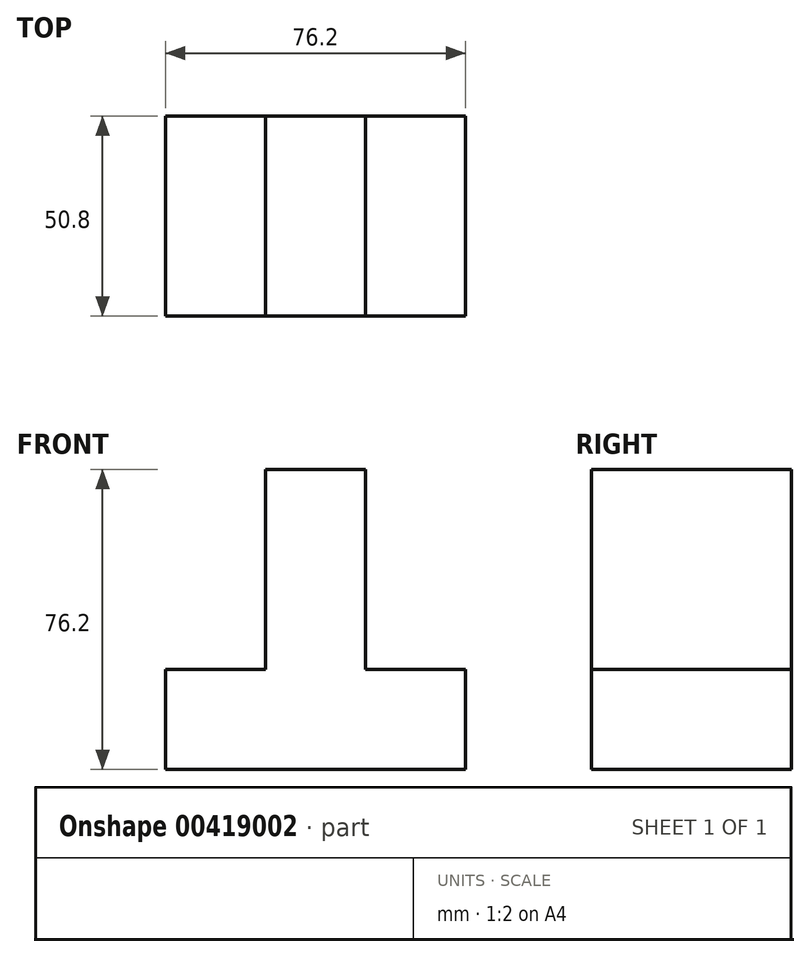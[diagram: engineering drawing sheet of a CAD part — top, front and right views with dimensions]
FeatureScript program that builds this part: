
annotation { "Feature Type Name" : "Feature", "Feature Type Description" : "" }
export const myFeature = defineFeature(function(context is Context, id is Id, definition is map)
    precondition{}
    {
        {
            var Q0;
            Q0=qCreatedBy(makeId("Front.planeOp"),FACE);
            var sketch = newSketch(context, id + "F0", { "sketchPlane" : qUnion([Q0])});
            skLineSegment(sketch, "E0", {"start": v(0, 0) * mm, "end": v(-76.2, 0) * mm});
            skLineSegment(sketch, "E1", {"start": v(-76.2, 0) * mm, "end": v(-76.2, 25.4) * mm});
            skLineSegment(sketch, "E2", {"start": v(-76.2, 25.4) * mm, "end": v(-50.8, 25.4) * mm});
            skLineSegment(sketch, "E3", {"start": v(-50.8, 25.4) * mm, "end": v(-50.8, 76.2) * mm});
            skLineSegment(sketch, "E4", {"start": v(0, 0) * mm, "end": v(0, 25.4) * mm});
            skLineSegment(sketch, "E5", {"start": v(0, 25.4) * mm, "end": v(-25.4, 25.4) * mm});
            skLineSegment(sketch, "E6", {"start": v(-25.4, 25.4) * mm, "end": v(-25.4, 76.2) * mm});
            skLineSegment(sketch, "E7", {"start": v(-25.4, 76.2) * mm, "end": v(-50.8, 76.2) * mm});
            skSolve(sketch);
        }
        {
            var Q0;
            Q0=makeQuery(id+"F0.imprint","IMPRINT",FACE,{"disambiguationData":[TD([[makeQuery(id+"F0.imprint","IMPRINT",EDGE,{"derivedFrom":sQuery(id+"F0.wireOp",EDGE,"E0")}),-1.0]])]});
            extrude(context, id + "F1", {"entities" : qUnion([Q0]), "depth" : 50.8 * mm});
        }
    });
